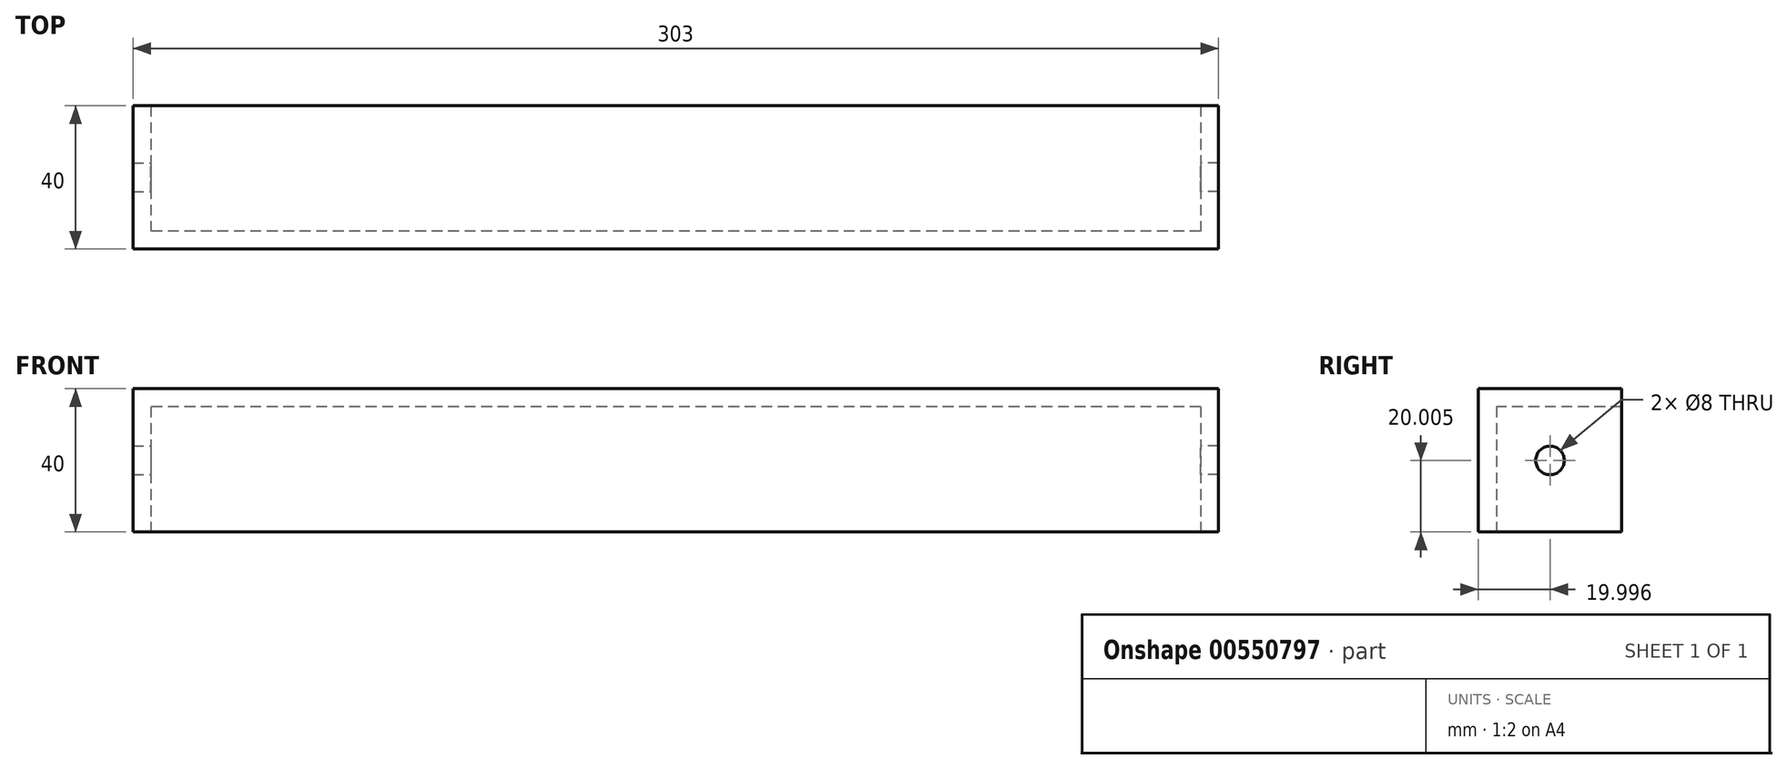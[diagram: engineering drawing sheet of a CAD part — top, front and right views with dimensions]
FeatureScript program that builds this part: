
annotation { "Feature Type Name" : "Feature", "Feature Type Description" : "" }
export const myFeature = defineFeature(function(context is Context, id is Id, definition is map)
    precondition{}
    {
        {
            var Q0;
            Q0=qCreatedBy(makeId("Right.planeOp"),FACE);
            var sketch = newSketch(context, id + "F0", { "sketchPlane" : qUnion([Q0])});
            skLineSegment(sketch, "E0", {"start": v(-7.97, -24.38) * mm, "end": v(-7.97, 15.62) * mm});
            skLineSegment(sketch, "E1", {"start": v(-7.97, 15.62) * mm, "end": v(32.03, 15.62) * mm});
            skLineSegment(sketch, "E2", {"start": v(32.03, 15.62) * mm, "end": v(32.03, 10.62) * mm});
            skLineSegment(sketch, "E3", {"start": v(32.03, 10.62) * mm, "end": v(-2.97, 10.62) * mm});
            skLineSegment(sketch, "E4", {"start": v(-2.97, 10.62) * mm, "end": v(-2.97, -24.38) * mm});
            skLineSegment(sketch, "E5", {"start": v(-2.97, -24.38) * mm, "end": v(-7.97, -24.38) * mm});
            skSolve(sketch);
        }
        {
            var Q0;
            Q0 = qSketchRegion(id + "F0", true);
            extrude(context, id + "F1", {"entities" : qUnion([Q0]), "depth" : 293 * mm, "offsetDistance" : 25 * mm});
        }
        {
            var Q0;
            Q0=makeQuery(id+"F1.opExtrude","CAP_FACE",FACE,{"disambiguationData":[OSD([sQuery(id+"F0.wireOp",EDGE,"E0"),sQuery(id+"F0.wireOp",EDGE,"E1"),sQuery(id+"F0.wireOp",EDGE,"E2"),sQuery(id+"F0.wireOp",EDGE,"E3"),sQuery(id+"F0.wireOp",EDGE,"E4"),sQuery(id+"F0.wireOp",EDGE,"E5")])],"isStart":false});
            var sketch = newSketch(context, id + "F2", { "sketchPlane" : qUnion([Q0])});
            skLineSegment(sketch, "E6.bottom", {"start": v(-7.97, -24.38) * mm, "end": v(32.03, -24.38) * mm});
            skLineSegment(sketch, "E6.top", {"start": v(-7.97, 15.62) * mm, "end": v(32.03, 15.62) * mm});
            skLineSegment(sketch, "E6.left", {"start": v(-7.97, -24.38) * mm, "end": v(-7.97, 15.62) * mm});
            skLineSegment(sketch, "E6.right", {"start": v(32.03, -24.38) * mm, "end": v(32.03, 15.62) * mm});
            skCircle(sketch, "E7", {"center": v(12.03, -4.38) * mm, "radius": 4 * mm});
            skPoint(sketch, "E7.centerSnap0", {"position": v(32.03, -4.38) * mm});
            skPoint(sketch, "E7.centerSnap1", {"position": v(12.03, 15.62) * mm});
            skSolve(sketch);
        }
        {
            var Q0;
            {var subQ1=sQuery(id+"F2.wireOp",EDGE,"E6.top");Q0=makeQuery(id+"F2.imprint","IMPRINT",FACE,{"disambiguationData":[TD([[makeQuery(id+"F2.imprint","IMPRINT",EDGE,{"derivedFrom":subQ1}),-1.0]])]});}
            var Q1;
            {var subQ4=makeQuery(id+"F1.opExtrude","CAP_EDGE",EDGE,{"disambiguationData":[OSD([sQuery(id+"F0.wireOp",EDGE,"E3")])],"isStart":false});Q1=makeQuery(id+"F2.imprint","IMPRINT",FACE,{"disambiguationData":[TD([[makeQuery(id+"F2.imprint","IMPRINT",EDGE,{"derivedFrom":subQ4}),1.0]])]});}
            extrude(context, id + "F3", {"entities" : qUnion([Q0, Q1]), "operationType" : NewBodyOperationType.ADD, "depth" : 5 * mm, "offsetDistance" : 25 * mm});
        }
        {
            var Q0;
            Q0=makeQuery(id+"F1.opExtrude","CAP_FACE",FACE,{"disambiguationData":[OSD([sQuery(id+"F0.wireOp",EDGE,"E0"),sQuery(id+"F0.wireOp",EDGE,"E1"),sQuery(id+"F0.wireOp",EDGE,"E2"),sQuery(id+"F0.wireOp",EDGE,"E3"),sQuery(id+"F0.wireOp",EDGE,"E4"),sQuery(id+"F0.wireOp",EDGE,"E5")])],"isStart":true});
            var sketch = newSketch(context, id + "F4", { "sketchPlane" : qUnion([Q0])});
            skLineSegment(sketch, "E8.bottom", {"start": v(-32.03, 15.62) * mm, "end": v(7.97, 15.62) * mm});
            skLineSegment(sketch, "E8.top", {"start": v(-32.03, -24.38) * mm, "end": v(7.97, -24.38) * mm});
            skLineSegment(sketch, "E8.left", {"start": v(-32.03, 15.62) * mm, "end": v(-32.03, -24.38) * mm});
            skLineSegment(sketch, "E8.right", {"start": v(7.97, 15.62) * mm, "end": v(7.97, -24.38) * mm});
            skCircle(sketch, "E9", {"center": v(-12.03, -4.38) * mm, "radius": 4 * mm});
            skPoint(sketch, "E9.centerSnap0", {"position": v(-12.03, 15.62) * mm});
            skPoint(sketch, "E9.centerSnap1", {"position": v(7.97, -4.38) * mm});
            skSolve(sketch);
        }
        {
            var Q0;
            Q0 = qSketchRegion(id + "F4", true);
            extrude(context, id + "F5", {"entities" : qUnion([Q0]), "operationType" : NewBodyOperationType.ADD, "depth" : 5 * mm, "offsetDistance" : 25 * mm});
        }
    });
